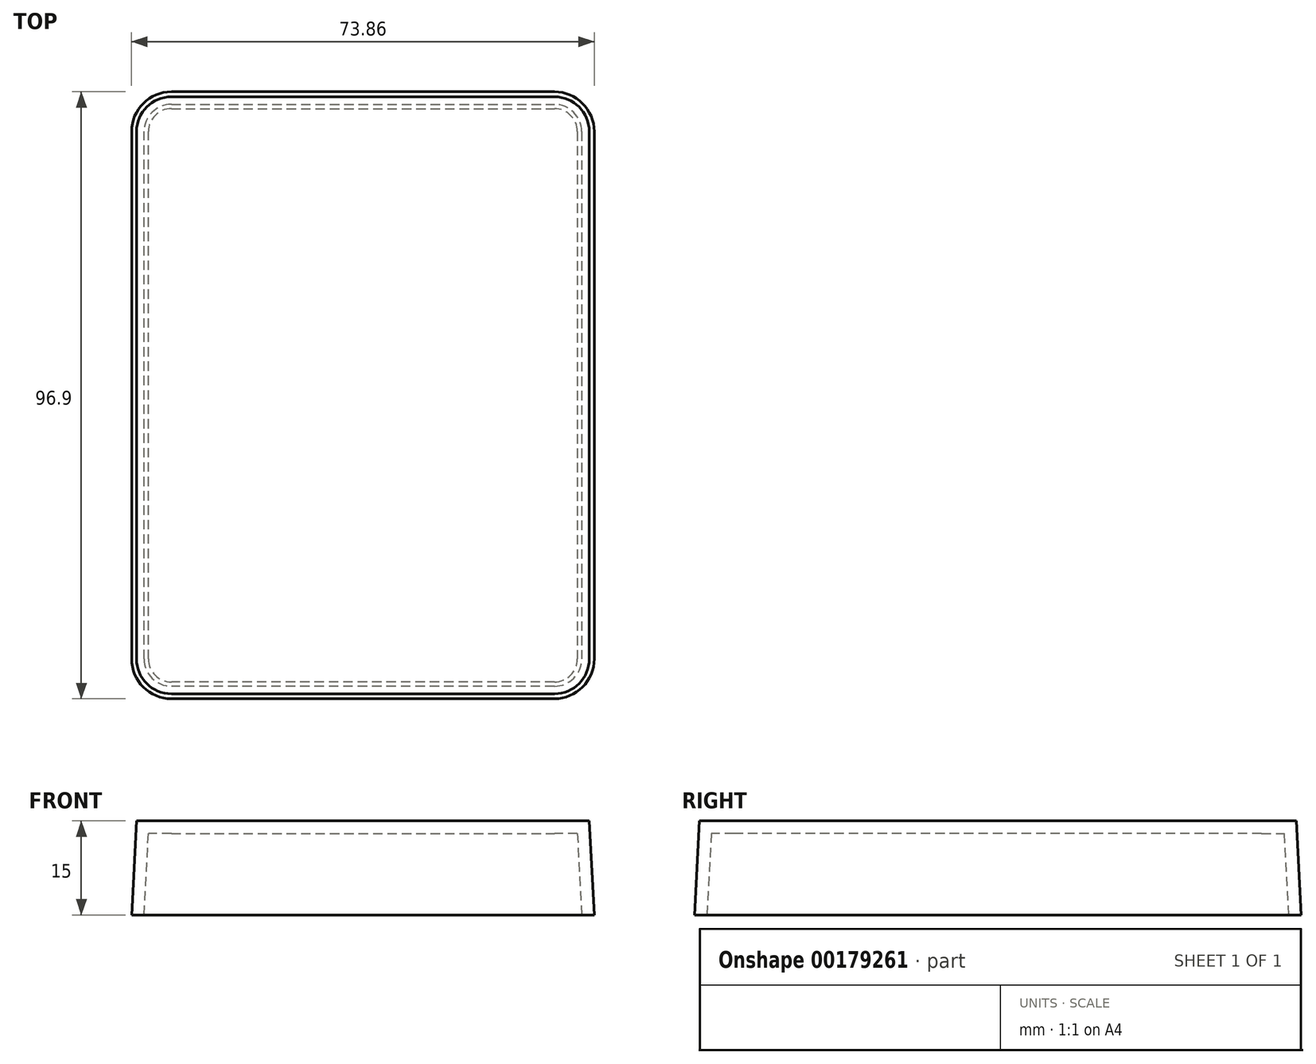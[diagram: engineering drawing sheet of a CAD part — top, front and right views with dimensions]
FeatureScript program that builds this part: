
annotation { "Feature Type Name" : "Feature", "Feature Type Description" : "" }
export const myFeature = defineFeature(function(context is Context, id is Id, definition is map)
    precondition{}
    {
        {
            var Q0;
            Q0=qCreatedBy(makeId("Top.planeOp"),FACE);
            var sketch = newSketch(context, id + "F0", { "sketchPlane" : qUnion([Q0])});
            skLineSegment(sketch, "E0.bottom", {"start": v(30.58, 48.45) * mm, "end": v(-30.58, 48.45) * mm});
            skLineSegment(sketch, "E0.top", {"start": v(30.58, -48.45) * mm, "end": v(-30.58, -48.45) * mm});
            skLineSegment(sketch, "E0.left", {"start": v(36.93, 42.1) * mm, "end": v(36.93, -42.1) * mm});
            skLineSegment(sketch, "E0.right", {"start": v(-36.93, 42.1) * mm, "end": v(-36.93, -42.1) * mm});
            skPoint(sketch, "E0.middle", {"position": v(0, 0) * mm});
            skPoint(sketch, "E1.visualSharp", {"position": v(-36.93, 48.45) * mm});
            skArc(sketch, "E1.filletArc", {"start": v(-30.58, 48.45) * mm, "mid": v(-35.07, 46.59) * mm, "end": v(-36.93, 42.1) * mm});
            skPoint(sketch, "E2.visualSharp", {"position": v(36.93, 48.45) * mm});
            skArc(sketch, "E2.filletArc", {"start": v(36.93, 42.1) * mm, "mid": v(35.07, 46.59) * mm, "end": v(30.58, 48.45) * mm});
            skPoint(sketch, "E3.visualSharp", {"position": v(36.93, -48.45) * mm});
            skArc(sketch, "E3.filletArc", {"start": v(30.58, -48.45) * mm, "mid": v(35.07, -46.59) * mm, "end": v(36.93, -42.1) * mm});
            skPoint(sketch, "E4.visualSharp", {"position": v(-36.93, -48.45) * mm});
            skArc(sketch, "E4.filletArc", {"start": v(-36.93, -42.1) * mm, "mid": v(-35.07, -46.59) * mm, "end": v(-30.58, -48.45) * mm});
            skSolve(sketch);
        }
        {
            var Q0;
            Q0=makeQuery(id+"F0.imprint","IMPRINT",FACE,{"disambiguationData":[TD([[makeQuery(id+"F0.imprint","IMPRINT",EDGE,{"derivedFrom":sQuery(id+"F0.wireOp",EDGE,"E0.bottom")}),1.0]])]});
            extrude(context, id + "F1", {"entities" : qUnion([Q0]), "depth" : 15 * mm, "hasDraft" : true, "draftAngle" : 3 * degree, "draftPullDirection" : true});
        }
        {
            var Q0;
            Q0=makeQuery(id+"F1.opExtrude","CAP_FACE",FACE,{"disambiguationData":[OSD([sQuery(id+"F0.wireOp",EDGE,"E0.bottom"),sQuery(id+"F0.wireOp",EDGE,"E0.top"),sQuery(id+"F0.wireOp",EDGE,"E0.left"),sQuery(id+"F0.wireOp",EDGE,"E0.right"),sQuery(id+"F0.wireOp",EDGE,"E1.filletArc"),sQuery(id+"F0.wireOp",EDGE,"E2.filletArc"),sQuery(id+"F0.wireOp",EDGE,"E3.filletArc"),sQuery(id+"F0.wireOp",EDGE,"E4.filletArc")])],"isStart":true});
            shell(context, id + "F2", {"entities" : qUnion([Q0]), "thickness" : 2 * mm});
        }
    });
